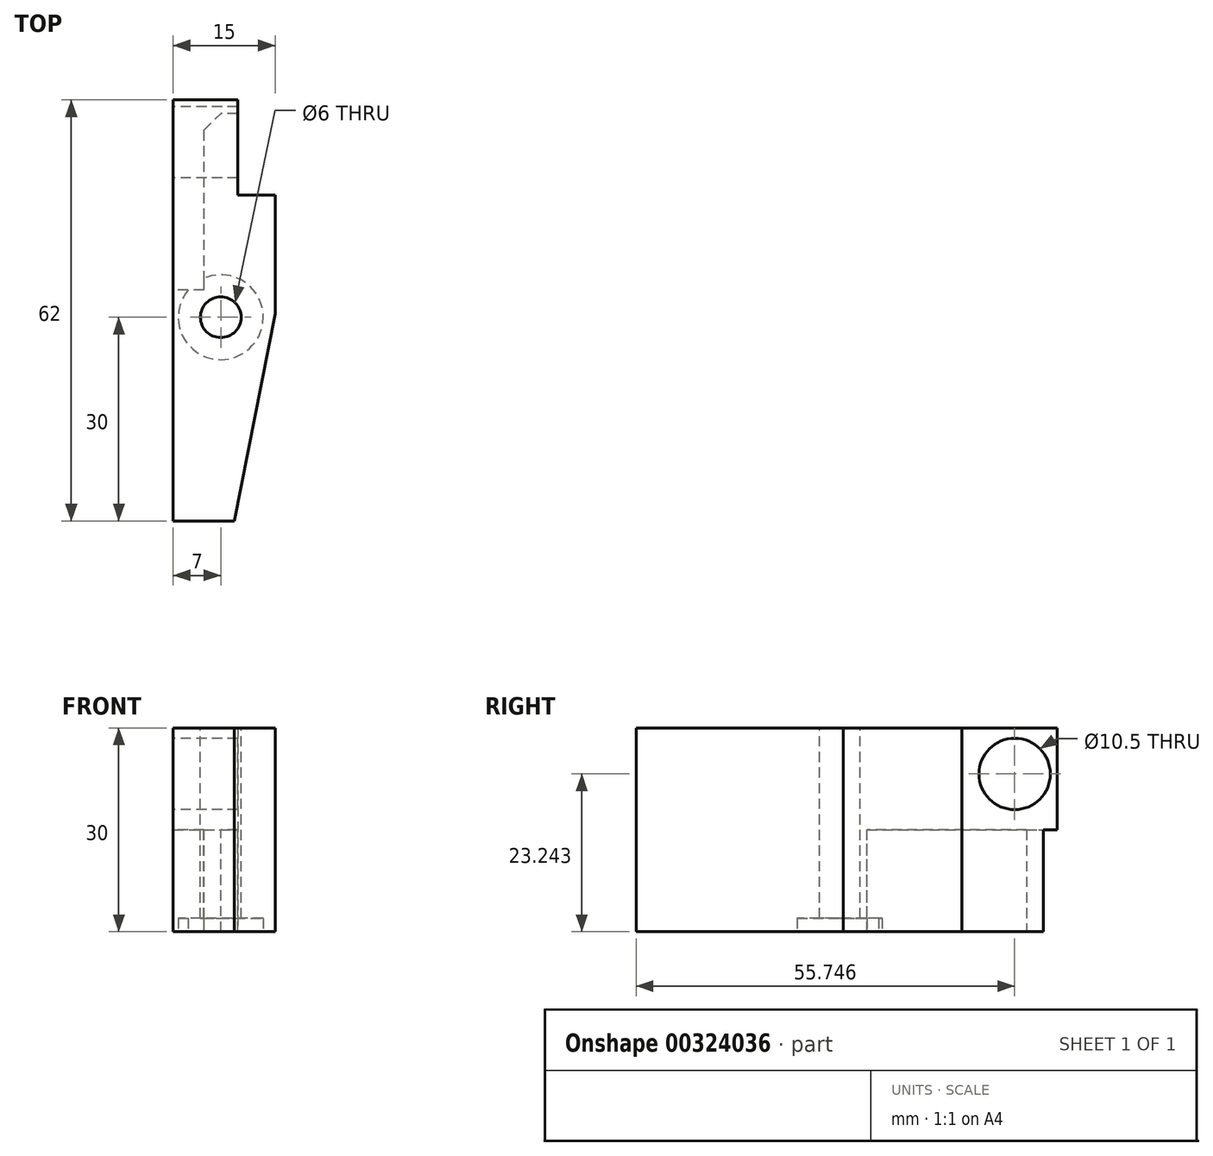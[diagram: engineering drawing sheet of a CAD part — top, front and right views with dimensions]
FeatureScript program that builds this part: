
annotation { "Feature Type Name" : "Feature", "Feature Type Description" : "" }
export const myFeature = defineFeature(function(context is Context, id is Id, definition is map)
    precondition{}
    {
        {
            var Q0;
            Q0=qCreatedBy(makeId("Top.planeOp"),FACE);
            var sketch = newSketch(context, id + "F0", { "sketchPlane" : qUnion([Q0])});
            skLineSegment(sketch, "E0", {"start": v(0, 0) * mm, "end": v(0, 62) * mm});
            skLineSegment(sketch, "E1", {"start": v(0, 62) * mm, "end": v(9.5, 62) * mm});
            skLineSegment(sketch, "E2", {"start": v(9.5, 62) * mm, "end": v(9.5, 48) * mm});
            skLineSegment(sketch, "E3", {"start": v(9.5, 48) * mm, "end": v(15, 48) * mm});
            skLineSegment(sketch, "E4", {"start": v(15, 48) * mm, "end": v(15, 30.5) * mm});
            skLineSegment(sketch, "E5", {"start": v(0, 0) * mm, "end": v(9, 0) * mm});
            skLineSegment(sketch, "E6", {"start": v(9, 0) * mm, "end": v(15, 30.5) * mm});
            skSolve(sketch);
        }
        {
            var Q0;
            Q0 = qSketchRegion(id + "F0", true);
            extrude(context, id + "F1", {"entities" : qUnion([Q0]), "depth" : 15 * mm});
        }
        {
            var Q0;
            Q0=makeQuery(id+"F1.opExtrude","CAP_FACE",FACE,{"disambiguationData":[OSD([sQuery(id+"F0.wireOp",EDGE,"E0"),sQuery(id+"F0.wireOp",EDGE,"E1"),sQuery(id+"F0.wireOp",EDGE,"E2"),sQuery(id+"F0.wireOp",EDGE,"E3"),sQuery(id+"F0.wireOp",EDGE,"E4"),sQuery(id+"F0.wireOp",EDGE,"E5"),sQuery(id+"F0.wireOp",EDGE,"E6")])],"isStart":true});
            var sketch = newSketch(context, id + "F2", { "sketchPlane" : qUnion([Q0])});
            skLineSegment(sketch, "E7", {"start": v(9.5, -60) * mm, "end": v(4.5, -60) * mm});
            skLineSegment(sketch, "E8", {"start": v(4.5, -60) * mm, "end": v(4.5, -34) * mm});
            skLineSegment(sketch, "E9", {"start": v(4.5, -34) * mm, "end": v(0, -34) * mm});
            skSolve(sketch);
        }
        {
            var Q0;
            Q0 = qSketchRegion(id + "F2", true);
            var Q1;
            {var subQ2=sQuery(id+"F2.wireOp",EDGE,"E7");Q1=makeQuery(id+"F2.imprint","IMPRINT",FACE,{"disambiguationData":[TD([[makeQuery(id+"F2.imprint","IMPRINT",EDGE,{"derivedFrom":subQ2}),-1.0]])]});}
            extrude(context, id + "F3", {"entities" : qUnion([Q0, Q1]), "operationType" : NewBodyOperationType.ADD, "depth" : 15 * mm});
        }
        {
            var Q0;
            Q0=makeQuery(id+"F3.opExtrude","SWEPT_EDGE",EDGE,{"disambiguationData":[OSD([sQuery(id+"F2.wireOp",EDGE,"E7"),sQuery(id+"F2.wireOp",EDGE,"E8")])]});
            chamfer(context, id + "F4", {"entities" : qUnion([Q0]), "width" : 2.5 * mm, "tangentPropagation" : true});
        }
        {
            var Q0;
            {var subQ0=sQuery(id+"F0.wireOp",EDGE,"E0");Q0=makeQuery(id+"F3.boolean.opBoolean","MERGE",FACE,{"derivedFrom":[makeQuery(id+"F1.opExtrude","SWEPT_FACE",FACE,{"disambiguationData":[OSD([subQ0])]}),makeQuery(id+"F3.opExtrude","SWEPT_FACE",FACE,{"disambiguationData":[OSD([subQ0])]})]});}
            var sketch = newSketch(context, id + "F5", { "sketchPlane" : qUnion([Q0])});
            skCircle(sketch, "E10", {"center": v(-55.75, 8.24) * mm, "radius": 5.25 * mm});
            skSolve(sketch);
        }
        {
            var Q0;
            Q0 = qSketchRegion(id + "F5", true);
            extrude(context, id + "F6", {"entities" : qUnion([Q0]), "operationType" : NewBodyOperationType.REMOVE, "oppositeDirection" : true, "depth" : 15 * mm});
        }
        {
            var Q0;
            Q0=makeQuery(id+"F1.opExtrude","CAP_FACE",FACE,{"disambiguationData":[OSD([sQuery(id+"F0.wireOp",EDGE,"E0"),sQuery(id+"F0.wireOp",EDGE,"E1"),sQuery(id+"F0.wireOp",EDGE,"E2"),sQuery(id+"F0.wireOp",EDGE,"E3"),sQuery(id+"F0.wireOp",EDGE,"E4"),sQuery(id+"F0.wireOp",EDGE,"E5"),sQuery(id+"F0.wireOp",EDGE,"E6")])],"isStart":false});
            var sketch = newSketch(context, id + "F7", { "sketchPlane" : qUnion([Q0])});
            skCircle(sketch, "E11", {"center": v(7, 30) * mm, "radius": 3 * mm});
            skSolve(sketch);
        }
        {
            var Q0;
            Q0=makeQuery(id+"F7.imprint","IMPRINT",FACE,{"disambiguationData":[TD([[makeQuery(id+"F7.imprint","IMPRINT",EDGE,{"derivedFrom":sQuery(id+"F7.wireOp",EDGE,"E11")}),1.0]])]});
            extrude(context, id + "F8", {"entities" : qUnion([Q0]), "operationType" : NewBodyOperationType.REMOVE, "oppositeDirection" : true, "depth" : 35 * mm});
        }
        {
            var Q0;
            Q0=makeQuery(id+"F3.opExtrude","CAP_FACE",FACE,{"disambiguationData":[OSD([sQuery(id+"F0.wireOp",EDGE,"E0"),sQuery(id+"F0.wireOp",EDGE,"E2"),sQuery(id+"F0.wireOp",EDGE,"E3"),sQuery(id+"F0.wireOp",EDGE,"E4"),sQuery(id+"F0.wireOp",EDGE,"E5"),sQuery(id+"F0.wireOp",EDGE,"E6"),sQuery(id+"F2.wireOp",EDGE,"E7"),sQuery(id+"F2.wireOp",EDGE,"E8"),sQuery(id+"F2.wireOp",EDGE,"E9")])],"isStart":false});
            var sketch = newSketch(context, id + "F9", { "sketchPlane" : qUnion([Q0])});
            skCircle(sketch, "E12", {"center": v(7, -30) * mm, "radius": 6.25 * mm});
            skSolve(sketch);
        }
        {
            var Q0;
            Q0 = qSketchRegion(id + "F9", true);
            extrude(context, id + "F10", {"entities" : qUnion([Q0]), "operationType" : NewBodyOperationType.REMOVE, "oppositeDirection" : true, "depth" : 2 * mm});
        }
    });
